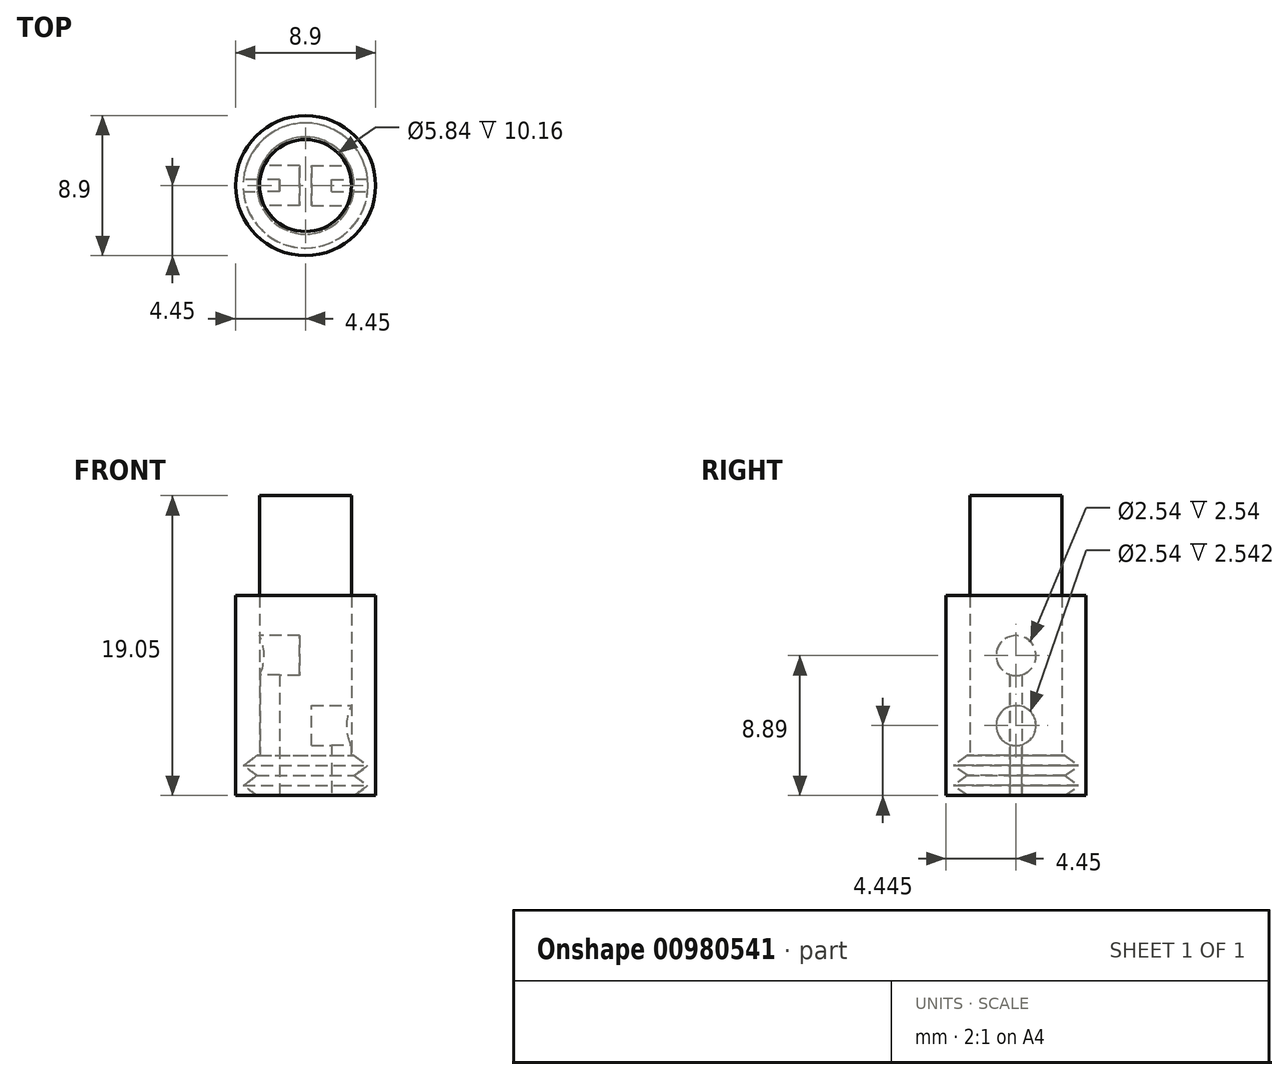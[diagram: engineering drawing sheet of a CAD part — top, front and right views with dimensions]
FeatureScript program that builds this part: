
annotation { "Feature Type Name" : "Feature", "Feature Type Description" : "" }
export const myFeature = defineFeature(function(context is Context, id is Id, definition is map)
    precondition{}
    {
        {
            var Q0;
            Q0=qCreatedBy(makeId("Front.planeOp"),FACE);
            var sketch = newSketch(context, id + "F0", { "sketchPlane" : qUnion([Q0])});
            skLineSegment(sketch, "E0", {"start": v(0, 0) * mm, "end": v(0, 19.05) * mm});
            skLineSegment(sketch, "E1", {"start": v(3.09, 2.54) * mm, "end": v(3.97, 1.9) * mm});
            skLineSegment(sketch, "E2", {"start": v(3.97, 1.9) * mm, "end": v(3.09, 1.27) * mm});
            skLineSegment(sketch, "E3", {"start": v(3.09, 1.27) * mm, "end": v(3.97, 0.64) * mm});
            skLineSegment(sketch, "E4", {"start": v(3.97, 0.63) * mm, "end": v(3.09, 0) * mm});
            skLineSegment(sketch, "E5", {"start": v(3.09, 0) * mm, "end": v(0, 0) * mm});
            skLineSegment(sketch, "E6", {"start": v(3.09, 2.54) * mm, "end": v(2.92, 2.54) * mm});
            skLineSegment(sketch, "E7", {"start": v(2.92, 2.54) * mm, "end": v(2.92, 19.05) * mm});
            skLineSegment(sketch, "E8", {"start": v(0, 19.05) * mm, "end": v(2.92, 19.05) * mm});
            skLineSegment(sketch, "E9", {"start": v(2.92, 12.7) * mm, "end": v(4.44, 12.7) * mm});
            skLineSegment(sketch, "E10", {"start": v(4.44, 12.7) * mm, "end": v(4.45, 0) * mm});
            skLineSegment(sketch, "E11", {"start": v(4.45, 0) * mm, "end": v(3.09, 0) * mm});
            skSolve(sketch);
        }
        {
            var Q0;
            Q0=makeQuery(id+"F0.imprint","IMPRINT",FACE,{"disambiguationData":[TD([[makeQuery(id+"F0.imprint","IMPRINT",EDGE,{"derivedFrom":sQuery(id+"F0.wireOp",EDGE,"E0")}),-1.0]])]});
            var Q1;
            Q1=sQuery(id+"F0.wireOp",EDGE,"E0");
            revolve(context, id + "F1", {"surfaceOperationType" : NewSurfaceOperationType.NEW, "entities" : qUnion([Q0]), "axis" : qUnion([Q1]), "revolveType" : RevolveType.FULL});
        }
        {
            var Q0;
            Q0=qCreatedBy(makeId("Right.planeOp"),FACE);
            cPlane(context, id + "F2", {"entities" : qUnion([Q0]), "cplaneType" : CPlaneType.OFFSET, "offset" : 2.92 * mm, "width" : 152.4 * mm, "height" : 152.4 * mm});
        }
        {
            var Q0;
            Q0=qCreatedBy(id+"F2.planeOp",FACE);
            var sketch = newSketch(context, id + "F3", { "sketchPlane" : qUnion([Q0])});
            skCircle(sketch, "E12", {"center": v(0, 4.45) * mm, "radius": 1.27 * mm});
            skLineSegment(sketch, "E13", {"start": v(-0.38, 3.23) * mm, "end": v(-0.38, 0) * mm});
            skLineSegment(sketch, "E14", {"start": v(-0.38, 0) * mm, "end": v(0.38, 0) * mm});
            skLineSegment(sketch, "E15", {"start": v(0.38, 0) * mm, "end": v(0.38, 3.23) * mm});
            skSolve(sketch);
        }
        {
            var Q0;
            {var subQ0=sQuery(id+"F3.wireOp",EDGE,"E12");var subQ1=makeQuery(id+"F3.imprint","INTERSECT",VERTEX,{"derivedFrom":[subQ0,sQuery(id+"F3.wireOp",EDGE,"E13")]});Q0=makeQuery(id+"F3.imprint","IMPRINT",FACE,{"disambiguationData":[TD([[makeQuery(id+"F3.imprint","IMPRINT",EDGE,{"disambiguationData":[TD([[subQ1,-1.0]])],"derivedFrom":subQ0}),1.0]])]});}
            extrude(context, id + "F4", {"entities" : qUnion([Q0]), "operationType" : NewBodyOperationType.REMOVE, "oppositeDirection" : true, "depth" : 2.54 * mm, "offsetDistance" : 25.4 * mm});
        }
        {
            var Q0;
            {var subQ0=sQuery(id+"F3.wireOp",EDGE,"E13");Q0=makeQuery(id+"F3.imprint","IMPRINT",FACE,{"disambiguationData":[TD([[makeQuery(id+"F3.imprint","IMPRINT",EDGE,{"derivedFrom":subQ0}),1.0]])]});}
            extrude(context, id + "F5", {"entities" : qUnion([Q0]), "operationType" : NewBodyOperationType.REMOVE, "oppositeDirection" : true, "depth" : 1.27 * mm, "offsetDistance" : 25.4 * mm, "hasSecondDirection" : true, "secondDirectionBound" : SecondDirectionBoundingType.THROUGH_ALL, "secondDirectionOppositeDirection" : false, "secondDirectionDepth" : 25.4 * mm});
        }
        {
            var Q0;
            Q0=qCreatedBy(makeId("Right.planeOp"),FACE);
            cPlane(context, id + "F6", {"entities" : qUnion([Q0]), "cplaneType" : CPlaneType.OFFSET, "offset" : 2.92 * mm, "oppositeDirection" : true, "width" : 152.4 * mm, "height" : 152.4 * mm});
        }
        {
            var Q0;
            Q0=qCreatedBy(id+"F6.planeOp",FACE);
            var sketch = newSketch(context, id + "F7", { "sketchPlane" : qUnion([Q0])});
            skCircle(sketch, "E16", {"center": v(0, 8.9) * mm, "radius": 1.27 * mm});
            skLineSegment(sketch, "E17", {"start": v(0.38, 7.68) * mm, "end": v(0.38, 0) * mm});
            skLineSegment(sketch, "E18", {"start": v(0.38, 0) * mm, "end": v(-0.38, 0) * mm});
            skLineSegment(sketch, "E19", {"start": v(-0.38, 0) * mm, "end": v(-0.38, 7.68) * mm});
            skSolve(sketch);
        }
        {
            var Q0;
            {var subQ0=sQuery(id+"F7.wireOp",EDGE,"E16");var subQ1=makeQuery(id+"F7.imprint","INTERSECT",VERTEX,{"derivedFrom":[subQ0,sQuery(id+"F7.wireOp",EDGE,"E17")]});Q0=makeQuery(id+"F7.imprint","IMPRINT",FACE,{"disambiguationData":[TD([[makeQuery(id+"F7.imprint","IMPRINT",EDGE,{"disambiguationData":[TD([[subQ1,1.0]])],"derivedFrom":subQ0}),1.0]])]});}
            extrude(context, id + "F8", {"entities" : qUnion([Q0]), "operationType" : NewBodyOperationType.REMOVE, "depth" : 2.54 * mm, "offsetDistance" : 25.4 * mm});
        }
        {
            var Q0;
            {var subQ0=sQuery(id+"F7.wireOp",EDGE,"E17");Q0=makeQuery(id+"F7.imprint","IMPRINT",FACE,{"disambiguationData":[TD([[makeQuery(id+"F7.imprint","IMPRINT",EDGE,{"derivedFrom":subQ0}),-1.0]])]});}
            extrude(context, id + "F9", {"entities" : qUnion([Q0]), "operationType" : NewBodyOperationType.REMOVE, "depth" : 1.27 * mm, "offsetDistance" : 25.4 * mm, "hasSecondDirection" : true, "secondDirectionBound" : SecondDirectionBoundingType.THROUGH_ALL, "secondDirectionOppositeDirection" : true, "secondDirectionDepth" : 25.4 * mm});
        }
        {
            var Q0;
            Q0=makeQuery(id+"F0.imprint","IMPRINT",FACE,{"disambiguationData":[TD([[makeQuery(id+"F0.imprint","IMPRINT",EDGE,{"derivedFrom":sQuery(id+"F0.wireOp",EDGE,"E1")}),1.0]])]});
            var Q1;
            Q1=sQuery(id+"F0.wireOp",EDGE,"E0");
            revolve(context, id + "F10", {"surfaceOperationType" : NewSurfaceOperationType.NEW, "entities" : qUnion([Q0]), "axis" : qUnion([Q1]), "revolveType" : RevolveType.FULL});
        }
    });
